# Revit family: 0042523 Sylvania Lighting Fixture ISOLINE  1690MM 4K MD UGR DA 8C
name_source: partatom
category: Lighting Fixtures
revit_build: Autodesk Revit 2018 (Build: 20170223_1515(x64)
units: mm (PartAtom-declared; Revit-internal decimal feet)

## family parameters
Cut with Voids When Loaded = No
Host = Face
Light Source = Yes
OmniClass Number = 23.80.70.00
OmniClass Title = Lighting
Part Type = Normal
Room Calculation Point = No
Round Connector Dimension = Use Diameter
Shared = No

## types (1)
- 0042523 ISOLINE  1690MM 4K MD UGR DA 8C
    Apparent Load = 56 VA
    Assembly Code = D5020200
    AssetType = Fixed
    ClassificationName = Uniclass2015
    ClassificationValue = EF_70_80
    Color Filter = 16777215
    Cost = 0 $
    Default Elevation = 1219 mm
    Description = Isoline LED linear DALI dimmable luminaire for industrial and commercial applications. 1690 mm lenght with medium optics provide homogenous light distribution for aisles and focus areas. Suitable for DALI Dimming. Aluminium housing, RAL 9016. Max + 35 °C operating temperature range, 4000 K, CRI 80, UGR <20, 3 SDMC. 56 W power consumption, 8800 lm luminous flux, 157 lm/W efficacy, 1690 mm x 62 mm x 59 mm (L x W x H) dimensions, IP20, IK03, DC 50/60 Hz, Class I. Lifespan L70:B50 60,000 hours.
    Dimming Lamp Color Temperature Shift = <None>
    DocumentationLiterature = http://www.sylvania-lighting.com
    DurationUnit = hours
    ElectricShockClassification = 157
    Emit Shape Visible in Rendering = No
    Emit from Circle Diameter = 610 mm
    ExpectedLife = 50000
    Height = 1000 mm  [stored 3.28084 ft]
    IfcExportAs = Class I
    IfcExportType = IfcLightFixtureType
    ImpactProtectionIndex = IfcLightFixtureType
    IngressProtection = IfcLightFixtureType
    InputNominalFrequency = 4000
    InputVoltage = 0
    LampColourRenderingIndex = 16500
    LampColourTemperature = LED
    LampMacAdamStep = 80
    LampNominalLuminous = 4000 K
    Length = 1690 mm  [stored 5.54462 ft]
    LightOutputRatio = LED
    LuminaireType = 0
    ManufacturerName = 157 lm/W
    Material = Feilo Sylvania
    Material_1_FEILO = <By Category>
    Material_2_FEILO = <By Category>
    Material_3_FEILO = <By Category>
    Material_4_FEILO = <By Category>
    Model = ISOLINE  1690MM 4K MD UGR DA 8C
    ModelNumber = 0042523
    ModelReference = ISOLINE  1690MM 4K MD UGR DA 8C
    Name = ISOLINE  1690MM 4K MD UGR DA 8C
    NominalDepth = 0 mm  [stored 0 ft]
    NominalHeight = 0 mm  [stored 0 ft]
    NominalLength = 62 mm
    Photometric Web File = 0042523.ies
    PowerConsumption = Lighting
    PowerFactor = 0
    Tilt Angle = 90.00°
    Type Image = <None>
    TypeName = ISOLINE  1690MM 4K MD UGR DA 8C
    URL = 0
    Voltage = 0 V
    WarrantyDescription = http://www.sylvania-lighting.com
    Width = 62 mm
    height = 59 mm
    spacer centres = 1000 mm  [stored 3.28084 ft]
    spacer height = 5 mm  [stored 0.0164042 ft]
    suspension height = 1000 mm  [stored 3.28084 ft]

note: [stored X ft] marks values corroborated as IEEE doubles in the binary element streams (Revit-internal decimal feet)

## geometry (parser evidence)
native form markers: Sweep x3
no freeform markers — native parametric forms only
